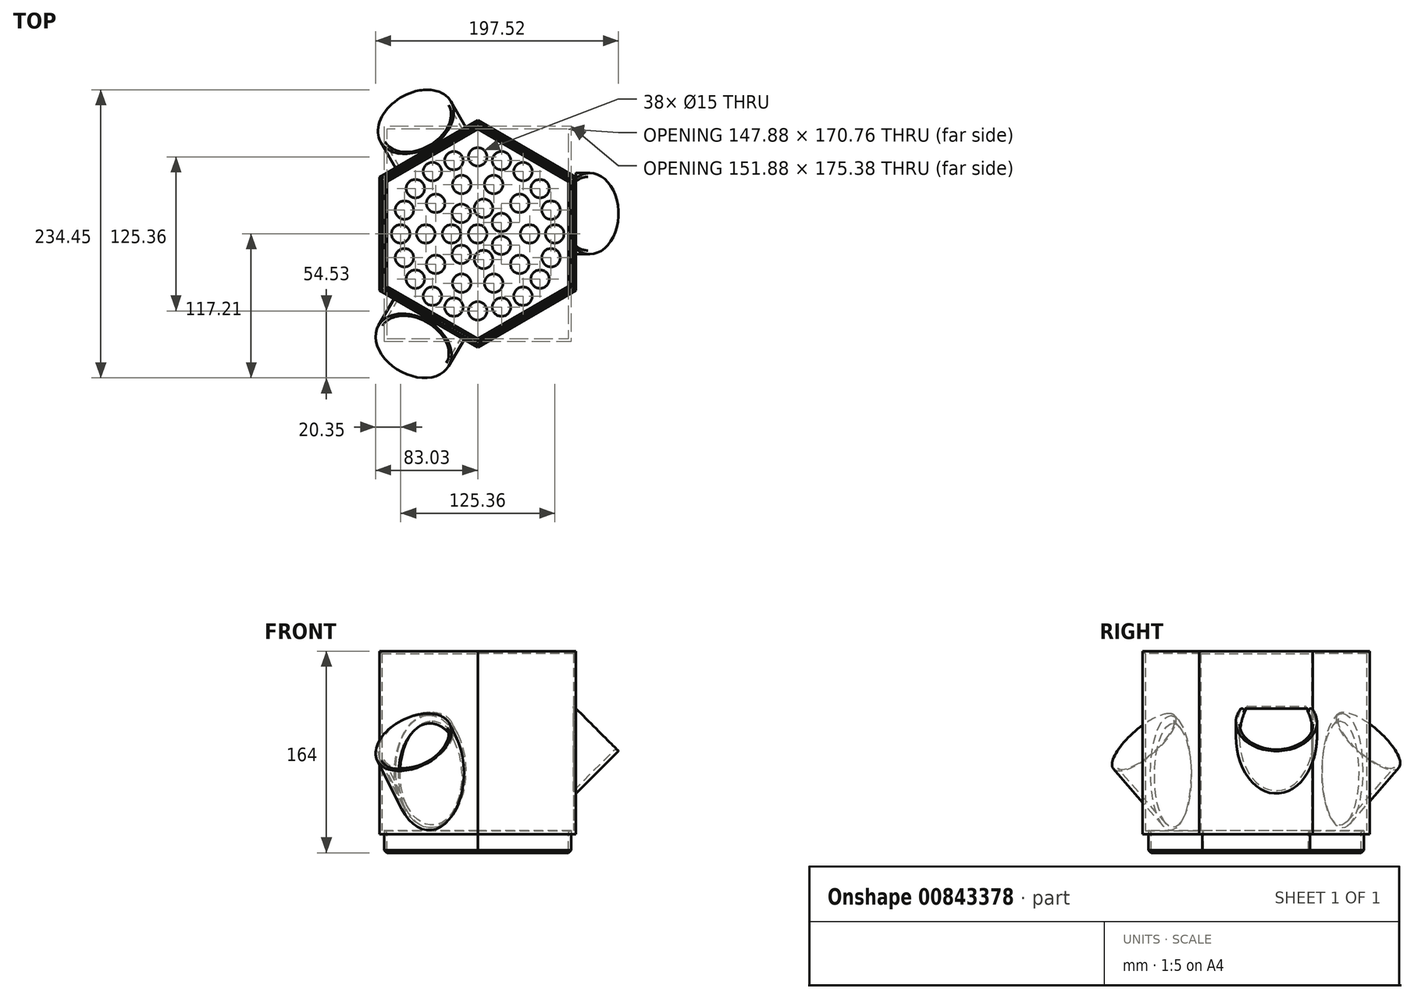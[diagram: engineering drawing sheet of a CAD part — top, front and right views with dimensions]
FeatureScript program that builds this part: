
annotation { "Feature Type Name" : "Feature", "Feature Type Description" : "" }
export const myFeature = defineFeature(function(context is Context, id is Id, definition is map)
    precondition{}
    {
        {
            var Q0;
            Q0=qCreatedBy(makeId("Top.planeOp"),FACE);
            var sketch = newSketch(context, id + "F0", { "sketchPlane" : qUnion([Q0])});
            skCircle(sketch, "E0.cCircle", {"center": v(0, 0) * mm, "radius": 77.94 * mm, "construction": true});
            skLineSegment(sketch, "E0.0", {"start": v(-77.94, -45) * mm, "end": v(-77.94, 45) * mm});
            skLineSegment(sketch, "E0.1", {"start": v(-77.94, 45) * mm, "end": v(0, 90) * mm});
            skLineSegment(sketch, "E0.2", {"start": v(0, 90) * mm, "end": v(77.94, 45) * mm});
            skLineSegment(sketch, "E0.3", {"start": v(77.94, 45) * mm, "end": v(77.94, -45) * mm});
            skLineSegment(sketch, "E0.4", {"start": v(77.94, -45) * mm, "end": v(0, -90) * mm});
            skLineSegment(sketch, "E0.5", {"start": v(0, -90) * mm, "end": v(-77.94, -45) * mm});
            skPoint(sketch, "E0.0.midPoint", {"position": v(-77.94, 0) * mm});
            skLineSegment(sketch, "E1.0", {"start": v(-79.94, -46.15) * mm, "end": v(-79.94, 46.15) * mm});
            skLineSegment(sketch, "E1.1", {"start": v(0, 92.3) * mm, "end": v(79.94, 46.15) * mm});
            skLineSegment(sketch, "E1.2", {"start": v(79.94, 46.15) * mm, "end": v(79.94, -46.15) * mm});
            skLineSegment(sketch, "E1.3", {"start": v(-79.94, 46.15) * mm, "end": v(0, 92.3) * mm});
            skLineSegment(sketch, "E1.4", {"start": v(79.94, -46.15) * mm, "end": v(0, -92.3) * mm});
            skLineSegment(sketch, "E1.5", {"start": v(0, -92.3) * mm, "end": v(-79.94, -46.15) * mm});
            skLineSegment(sketch, "E2.0", {"start": v(73.94, -42.7) * mm, "end": v(0, -85.38) * mm});
            skLineSegment(sketch, "E2.1", {"start": v(-73.94, -42.7) * mm, "end": v(-73.94, 42.7) * mm});
            skLineSegment(sketch, "E2.2", {"start": v(-73.94, 42.7) * mm, "end": v(0, 85.38) * mm});
            skLineSegment(sketch, "E2.3", {"start": v(0, -85.38) * mm, "end": v(-73.94, -42.7) * mm});
            skLineSegment(sketch, "E2.4", {"start": v(0, 85.38) * mm, "end": v(73.94, 42.7) * mm});
            skLineSegment(sketch, "E2.5", {"start": v(73.94, 42.7) * mm, "end": v(73.94, -42.7) * mm});
            skLineSegment(sketch, "E3.0", {"start": v(75.94, 43.85) * mm, "end": v(75.94, -43.85) * mm});
            skLineSegment(sketch, "E3.1", {"start": v(0, -87.7) * mm, "end": v(-75.94, -43.85) * mm});
            skLineSegment(sketch, "E3.2", {"start": v(-75.94, -43.85) * mm, "end": v(-75.94, 43.85) * mm});
            skLineSegment(sketch, "E3.3", {"start": v(75.94, -43.85) * mm, "end": v(0, -87.7) * mm});
            skLineSegment(sketch, "E3.4", {"start": v(-75.94, 43.85) * mm, "end": v(0, 87.7) * mm});
            skLineSegment(sketch, "E3.5", {"start": v(0, 87.7) * mm, "end": v(75.94, 43.85) * mm});
            skCircle(sketch, "E4", {"center": v(0, 0) * mm, "radius": 7.5 * mm});
            skLineSegment(sketch, "E5", {"start": v(0, 0) * mm, "end": v(-77.94, 0) * mm, "construction": true});
            skCircle(sketch, "E6", {"center": v(-21.35, 0) * mm, "radius": 7.5 * mm});
            skCircle(sketch, "E7", {"center": v(-62.68, 0) * mm, "radius": 7.5 * mm});
            skCircle(sketch, "E8", {"center": v(-42.22, 0) * mm, "radius": 7.5 * mm});
            skCircle(sketch, "E9.1.0", {"center": v(-13.31, -16.7) * mm, "radius": 7.5 * mm});
            skCircle(sketch, "E9.2.0", {"center": v(4.75, -20.82) * mm, "radius": 7.5 * mm});
            skCircle(sketch, "E9.3.0", {"center": v(19.24, -9.27) * mm, "radius": 7.5 * mm});
            skCircle(sketch, "E9.4.0", {"center": v(19.24, 9.27) * mm, "radius": 7.5 * mm});
            skCircle(sketch, "E9.5.0", {"center": v(4.75, 20.82) * mm, "radius": 7.5 * mm});
            skCircle(sketch, "E9.6.0", {"center": v(-13.31, 16.7) * mm, "radius": 7.5 * mm});
            skCircle(sketch, "E10.1.0", {"center": v(-34.16, -24.82) * mm, "radius": 7.5 * mm});
            skCircle(sketch, "E10.2.0", {"center": v(-13.05, -40.15) * mm, "radius": 7.5 * mm});
            skCircle(sketch, "E10.3.0", {"center": v(13.05, -40.15) * mm, "radius": 7.5 * mm});
            skCircle(sketch, "E10.4.0", {"center": v(34.16, -24.82) * mm, "radius": 7.5 * mm});
            skCircle(sketch, "E10.5.0", {"center": v(42.22, 0) * mm, "radius": 7.5 * mm});
            skCircle(sketch, "E10.6.0", {"center": v(34.16, 24.82) * mm, "radius": 7.5 * mm});
            skCircle(sketch, "E10.7.0", {"center": v(13.05, 40.15) * mm, "radius": 7.5 * mm});
            skCircle(sketch, "E10.8.0", {"center": v(-13.05, 40.15) * mm, "radius": 7.5 * mm});
            skCircle(sketch, "E10.9.0", {"center": v(-34.16, 24.82) * mm, "radius": 7.5 * mm});
            skCircle(sketch, "E11.1.0", {"center": v(-59.61, -19.37) * mm, "radius": 7.5 * mm});
            skCircle(sketch, "E11.2.0", {"center": v(-50.7, -36.84) * mm, "radius": 7.5 * mm});
            skCircle(sketch, "E11.3.0", {"center": v(-36.84, -50.7) * mm, "radius": 7.5 * mm});
            skCircle(sketch, "E11.4.0", {"center": v(-19.37, -59.61) * mm, "radius": 7.5 * mm});
            skCircle(sketch, "E11.5.0", {"center": v(0, -62.68) * mm, "radius": 7.5 * mm});
            skCircle(sketch, "E11.6.0", {"center": v(19.37, -59.61) * mm, "radius": 7.5 * mm});
            skCircle(sketch, "E11.7.0", {"center": v(36.84, -50.7) * mm, "radius": 7.5 * mm});
            skCircle(sketch, "E11.8.0", {"center": v(50.7, -36.84) * mm, "radius": 7.5 * mm});
            skCircle(sketch, "E11.9.0", {"center": v(59.61, -19.37) * mm, "radius": 7.5 * mm});
            skCircle(sketch, "E12.1.10.0", {"center": v(62.68, 0) * mm, "radius": 7.5 * mm});
            skCircle(sketch, "E12.1.11.0", {"center": v(59.61, 19.37) * mm, "radius": 7.5 * mm});
            skCircle(sketch, "E12.1.12.0", {"center": v(50.7, 36.84) * mm, "radius": 7.5 * mm});
            skCircle(sketch, "E12.1.13.0", {"center": v(36.84, 50.7) * mm, "radius": 7.5 * mm});
            skCircle(sketch, "E12.1.14.0", {"center": v(19.37, 59.61) * mm, "radius": 7.5 * mm});
            skCircle(sketch, "E12.1.15.0", {"center": v(0, 62.68) * mm, "radius": 7.5 * mm});
            skCircle(sketch, "E12.1.16.0", {"center": v(-19.37, 59.61) * mm, "radius": 7.5 * mm});
            skCircle(sketch, "E12.1.17.0", {"center": v(-36.84, 50.7) * mm, "radius": 7.5 * mm});
            skCircle(sketch, "E12.1.18.0", {"center": v(-50.7, 36.84) * mm, "radius": 7.5 * mm});
            skCircle(sketch, "E12.1.19.0", {"center": v(-59.61, 19.37) * mm, "radius": 7.5 * mm});
            skSolve(sketch);
        }
        {
            var Q0;
            Q0 = qSketchRegion(id + "F0", true);
            extrude(context, id + "F1", {"entities" : qUnion([Q0]), "depth" : 150 * mm, "offsetDistance" : 25 * mm});
        }
        {
            var Q0;
            Q0=makeQuery(id+"F1.opExtrude","SWEPT_FACE",FACE,{"disambiguationData":[OSD([sQuery(id+"F0.wireOp",EDGE,"E1.2")])]});
            cPlane(context, id + "F2", {"entities" : qUnion([Q0]), "cplaneType" : CPlaneType.OFFSET, "offset" : 25 * mm, "width" : 150 * mm, "height" : 150 * mm});
        }
        {
            var Q0;
            Q0=qCreatedBy(id+"F2.planeOp",FACE);
            var sketch = newSketch(context, id + "F3", { "sketchPlane" : qUnion([Q0])});
            skLineSegment(sketch, "E13", {"start": v(-46.09, 77.36) * mm, "end": v(45.67, 77.36) * mm, "construction": true});
            skSolve(sketch);
        }
        {
            var Q0;
            Q0=sQuery(id+"F3.wireOp",EDGE,"E13");
            cPlane(context, id + "F4", {"entities" : qUnion([Q0]), "cplaneType" : CPlaneType.LINE_ANGLE, "offset" : 25 * mm, "angle" : 45 * degree, "width" : 150 * mm, "height" : 150 * mm});
        }
        {
            var Q0;
            Q0=qCreatedBy(id+"F4.planeOp",FACE);
            var sketch = newSketch(context, id + "F5", { "sketchPlane" : qUnion([Q0])});
            skCircle(sketch, "E14", {"center": v(16.48, 0) * mm, "radius": 30 * mm});
            skCircle(sketch, "E15.0", {"center": v(16.48, 0) * mm, "radius": 33 * mm});
            skSolve(sketch);
        }
        {
            var Q0;
            Q0=makeQuery(id+"F5.imprint","IMPRINT",FACE,{"disambiguationData":[TD([[makeQuery(id+"F5.imprint","IMPRINT",EDGE,{"derivedFrom":sQuery(id+"F5.wireOp",EDGE,"E14")}),-1.0]])]});
            var Q1;
            Q1=makeQuery(id+"F1.opExtrude","SWEPT_FACE",FACE,{"disambiguationData":[OSD([sQuery(id+"F0.wireOp",EDGE,"E1.2")])]});
            extrude(context, id + "F6", {"entities" : qUnion([Q0]), "operationType" : NewBodyOperationType.ADD, "endBound" : BoundingType.UP_TO_SURFACE, "oppositeDirection" : true, "depth" : 25 * mm, "endBoundEntityFace" : qUnion([Q1]), "offsetDistance" : 25 * mm});
        }
        {
            var Q0;
            Q0=makeQuery(id+"F5.imprint","IMPRINT",FACE,{"disambiguationData":[TD([[makeQuery(id+"F5.imprint","IMPRINT",EDGE,{"derivedFrom":sQuery(id+"F5.wireOp",EDGE,"E14")}),1.0]])]});
            var Q1;
            Q1=makeQuery(id+"F1.opExtrude","SWEPT_FACE",FACE,{"disambiguationData":[OSD([sQuery(id+"F0.wireOp",EDGE,"E0.3")])]});
            extrude(context, id + "F7", {"entities" : qUnion([Q0]), "operationType" : NewBodyOperationType.REMOVE, "endBound" : BoundingType.UP_TO_SURFACE, "oppositeDirection" : true, "depth" : 25 * mm, "endBoundEntityFace" : qUnion([Q1]), "offsetDistance" : 25 * mm});
        }
        {
            var Q0;
            Q0=makeQuery(id+"F1.opExtrude","SWEPT_FACE",FACE,{"disambiguationData":[OSD([sQuery(id+"F0.wireOp",EDGE,"E1.3")])]});
            cPlane(context, id + "F8", {"entities" : qUnion([Q0]), "cplaneType" : CPlaneType.OFFSET, "offset" : 25 * mm, "width" : 150 * mm, "height" : 150 * mm});
        }
        {
            var Q0;
            Q0=qCreatedBy(id+"F8.planeOp",FACE);
            var sketch = newSketch(context, id + "F9", { "sketchPlane" : qUnion([Q0])});
            skLineSegment(sketch, "E16", {"start": v(-47.86, 75) * mm, "end": v(44.27, 75) * mm, "construction": true});
            skSolve(sketch);
        }
        {
            var Q0;
            Q0=sQuery(id+"F9.wireOp",EDGE,"E16");
            cPlane(context, id + "F10", {"entities" : qUnion([Q0]), "cplaneType" : CPlaneType.LINE_ANGLE, "offset" : 25 * mm, "angle" : 45 * degree, "oppositeDirection" : true, "width" : 150 * mm, "height" : 150 * mm});
        }
        {
            var Q0;
            Q0=qCreatedBy(id+"F10.planeOp",FACE);
            var sketch = newSketch(context, id + "F11", { "sketchPlane" : qUnion([Q0])});
            skCircle(sketch, "E17", {"center": v(-5.63, -19.23) * mm, "radius": 30 * mm});
            skCircle(sketch, "E18.0", {"center": v(-5.63, -19.23) * mm, "radius": 33 * mm});
            skSolve(sketch);
        }
        {
            var Q0;
            Q0 = qSketchRegion(id + "F11", true);
            var Q1;
            Q1=makeQuery(id+"F1.opExtrude","SWEPT_FACE",FACE,{"disambiguationData":[OSD([sQuery(id+"F0.wireOp",EDGE,"E1.3")])]});
            extrude(context, id + "F12", {"entities" : qUnion([Q0]), "operationType" : NewBodyOperationType.ADD, "endBound" : BoundingType.UP_TO_SURFACE, "depth" : 25 * mm, "endBoundEntityFace" : qUnion([Q1]), "offsetDistance" : 25 * mm});
        }
        {
            var Q0;
            Q0=makeQuery(id+"F11.imprint","IMPRINT",FACE,{"disambiguationData":[TD([[makeQuery(id+"F11.imprint","IMPRINT",EDGE,{"derivedFrom":sQuery(id+"F11.wireOp",EDGE,"E17")}),1.0]])]});
            var Q1;
            Q1=makeQuery(id+"F1.opExtrude","SWEPT_FACE",FACE,{"disambiguationData":[OSD([sQuery(id+"F0.wireOp",EDGE,"E0.1")])]});
            extrude(context, id + "F13", {"entities" : qUnion([Q0]), "operationType" : NewBodyOperationType.REMOVE, "endBound" : BoundingType.UP_TO_SURFACE, "depth" : 25 * mm, "endBoundEntityFace" : qUnion([Q1]), "offsetDistance" : 25 * mm});
        }
        {
            var Q0;
            Q0=makeQuery(id+"F1.opExtrude","SWEPT_FACE",FACE,{"disambiguationData":[OSD([sQuery(id+"F0.wireOp",EDGE,"E1.5")])]});
            cPlane(context, id + "F14", {"entities" : qUnion([Q0]), "cplaneType" : CPlaneType.OFFSET, "offset" : 25 * mm, "width" : 150 * mm, "height" : 150 * mm});
        }
        {
            var Q0;
            Q0=qCreatedBy(id+"F14.planeOp",FACE);
            var sketch = newSketch(context, id + "F15", { "sketchPlane" : qUnion([Q0])});
            skLineSegment(sketch, "E19", {"start": v(-42.7, 75) * mm, "end": v(45.48, 75) * mm, "construction": true});
            skSolve(sketch);
        }
        {
            var Q0;
            Q0=sQuery(id+"F15.wireOp",EDGE,"E19");
            cPlane(context, id + "F16", {"entities" : qUnion([Q0]), "cplaneType" : CPlaneType.LINE_ANGLE, "offset" : 25 * mm, "angle" : 315 * degree, "width" : 150 * mm, "height" : 150 * mm});
        }
        {
            var Q0;
            Q0=qCreatedBy(id+"F16.planeOp",FACE);
            var sketch = newSketch(context, id + "F17", { "sketchPlane" : qUnion([Q0])});
            skCircle(sketch, "E20", {"center": v(-7.67, 19.81) * mm, "radius": 30 * mm});
            skCircle(sketch, "E21.0", {"center": v(-7.67, 19.81) * mm, "radius": 33 * mm});
            skSolve(sketch);
        }
        {
            var Q0;
            Q0 = qSketchRegion(id + "F17", true);
            var Q1;
            Q1=makeQuery(id+"F1.opExtrude","SWEPT_FACE",FACE,{"disambiguationData":[OSD([sQuery(id+"F0.wireOp",EDGE,"E1.5")])]});
            extrude(context, id + "F18", {"entities" : qUnion([Q0]), "operationType" : NewBodyOperationType.ADD, "endBound" : BoundingType.UP_TO_SURFACE, "depth" : 25 * mm, "endBoundEntityFace" : qUnion([Q1]), "offsetDistance" : 25 * mm});
        }
        {
            var Q0;
            Q0=makeQuery(id+"F17.imprint","IMPRINT",FACE,{"disambiguationData":[TD([[makeQuery(id+"F17.imprint","IMPRINT",EDGE,{"derivedFrom":sQuery(id+"F17.wireOp",EDGE,"E20")}),1.0]])]});
            var Q1;
            Q1=makeQuery(id+"F1.opExtrude","SWEPT_FACE",FACE,{"disambiguationData":[OSD([sQuery(id+"F0.wireOp",EDGE,"E0.5")])]});
            extrude(context, id + "F19", {"entities" : qUnion([Q0]), "operationType" : NewBodyOperationType.REMOVE, "endBound" : BoundingType.UP_TO_SURFACE, "depth" : 25 * mm, "endBoundEntityFace" : qUnion([Q1]), "offsetDistance" : 25 * mm});
        }
        {
            var Q0;
            Q0=makeQuery(id+"F0.imprint","IMPRINT",FACE,{"disambiguationData":[TD([[makeQuery(id+"F0.imprint","IMPRINT",EDGE,{"derivedFrom":sQuery(id+"F0.wireOp",EDGE,"E0.0")}),-1.0]])]});
            extrude(context, id + "F20", {"entities" : qUnion([Q0]), "operationType" : NewBodyOperationType.ADD, "depth" : 3 * mm, "offsetDistance" : 25 * mm});
        }
        {
            var Q0;
            Q0=makeQuery(id+"F0.imprint","IMPRINT",FACE,{"disambiguationData":[TD([[makeQuery(id+"F0.imprint","IMPRINT",EDGE,{"derivedFrom":sQuery(id+"F0.wireOp",EDGE,"E2.0")}),1.0]])]});
            extrude(context, id + "F21", {"entities" : qUnion([Q0]), "oppositeDirection" : true, "depth" : 15 * mm, "offsetDistance" : 25 * mm});
        }
        {
            var Q0;
            Q0=makeQuery(id+"F0.imprint","IMPRINT",FACE,{"disambiguationData":[TD([[makeQuery(id+"F0.imprint","IMPRINT",EDGE,{"derivedFrom":sQuery(id+"F0.wireOp",EDGE,"E2.0")}),-1.0]])]});
            extrude(context, id + "F22", {"entities" : qUnion([Q0]), "operationType" : NewBodyOperationType.ADD, "oppositeDirection" : true, "depth" : 15 * mm, "offsetDistance" : 25 * mm});
        }
        {
            var Q0;
            Q0=makeQuery(id+"F0.imprint","IMPRINT",FACE,{"disambiguationData":[TD([[makeQuery(id+"F0.imprint","IMPRINT",EDGE,{"derivedFrom":sQuery(id+"F0.wireOp",EDGE,"E2.0")}),-1.0]])]});
            extrude(context, id + "F23", {"entities" : qUnion([Q0]), "operationType" : NewBodyOperationType.REMOVE, "oppositeDirection" : true, "depth" : 13 * mm, "offsetDistance" : 25 * mm});
        }
        {
            var Q0;
            Q0=makeQuery(id+"F0.imprint","IMPRINT",FACE,{"disambiguationData":[TD([[makeQuery(id+"F0.imprint","IMPRINT",EDGE,{"derivedFrom":sQuery(id+"F0.wireOp",EDGE,"E2.0")}),1.0]])]});
            extrude(context, id + "F24", {"entities" : qUnion([Q0]), "depth" : 3 * mm, "offsetDistance" : 25 * mm});
        }
        {
            var Q0;
            Q0=makeQuery(id+"F1.opExtrude","CAP_EDGE",EDGE,{"disambiguationData":[OSD([sQuery(id+"F0.wireOp",EDGE,"E0.3")])],"isStart":false});
            var Q1;
            Q1=makeQuery(id+"F1.opExtrude","CAP_EDGE",EDGE,{"disambiguationData":[OSD([sQuery(id+"F0.wireOp",EDGE,"E0.4")])],"isStart":false});
            var Q2;
            Q2=makeQuery(id+"F1.opExtrude","CAP_EDGE",EDGE,{"disambiguationData":[OSD([sQuery(id+"F0.wireOp",EDGE,"E0.5")])],"isStart":false});
            var Q3;
            Q3=makeQuery(id+"F1.opExtrude","CAP_EDGE",EDGE,{"disambiguationData":[OSD([sQuery(id+"F0.wireOp",EDGE,"E0.0")])],"isStart":false});
            var Q4;
            Q4=makeQuery(id+"F1.opExtrude","CAP_EDGE",EDGE,{"disambiguationData":[OSD([sQuery(id+"F0.wireOp",EDGE,"E0.1")])],"isStart":false});
            var Q5;
            Q5=makeQuery(id+"F1.opExtrude","CAP_EDGE",EDGE,{"disambiguationData":[OSD([sQuery(id+"F0.wireOp",EDGE,"E0.2")])],"isStart":false});
            chamfer(context, id + "F25", {"entities" : qUnion([Q0, Q1, Q2, Q3, Q4, Q5]), "width" : 3 * mm, "tangentPropagation" : true});
        }
        {
            var Q0;
            Q0=makeQuery(id+"F12.opExtrude","CAP_EDGE",EDGE,{"disambiguationData":[OSD([sQuery(id+"F11.wireOp",EDGE,"E17")])],"isStart":true});
            var Q1;
            Q1=makeQuery(id+"F18.opExtrude","CAP_EDGE",EDGE,{"disambiguationData":[OSD([sQuery(id+"F17.wireOp",EDGE,"E20")])],"isStart":true});
            var Q2;
            Q2=makeQuery(id+"F6.opExtrude","CAP_EDGE",EDGE,{"disambiguationData":[OSD([sQuery(id+"F5.wireOp",EDGE,"E14")])],"isStart":true});
            var Q3;
            Q3=makeQuery(id+"F24.opExtrude","CAP_EDGE",EDGE,{"disambiguationData":[OSD([sQuery(id+"F0.wireOp",EDGE,"E2.5")])],"isStart":false});
            var Q4;
            Q4=makeQuery(id+"F24.opExtrude","CAP_EDGE",EDGE,{"disambiguationData":[OSD([sQuery(id+"F0.wireOp",EDGE,"E2.0")])],"isStart":false});
            var Q5;
            Q5=makeQuery(id+"F24.opExtrude","CAP_EDGE",EDGE,{"disambiguationData":[OSD([sQuery(id+"F0.wireOp",EDGE,"E2.4")])],"isStart":false});
            var Q6;
            Q6=makeQuery(id+"F24.opExtrude","CAP_EDGE",EDGE,{"disambiguationData":[OSD([sQuery(id+"F0.wireOp",EDGE,"E2.1")])],"isStart":false});
            var Q7;
            Q7=makeQuery(id+"F24.opExtrude","CAP_EDGE",EDGE,{"disambiguationData":[OSD([sQuery(id+"F0.wireOp",EDGE,"E2.2")])],"isStart":false});
            var Q8;
            Q8=makeQuery(id+"F24.opExtrude","CAP_EDGE",EDGE,{"disambiguationData":[OSD([sQuery(id+"F0.wireOp",EDGE,"E2.3")])],"isStart":false});
            fillet(context, id + "F26", {"entities" : qUnion([Q0, Q1, Q2, Q3, Q4, Q5, Q6, Q7, Q8]), "radius" : 2 * mm, "tangentPropagation" : true, "allowEdgeOverflow" : false});
        }
        {
            var Q0;
            Q0=makeQuery(id+"F21.opExtrude","CAP_EDGE",EDGE,{"disambiguationData":[OSD([sQuery(id+"F0.wireOp",EDGE,"E3.0")])],"isStart":false});
            var Q1;
            Q1=makeQuery(id+"F21.opExtrude","CAP_EDGE",EDGE,{"disambiguationData":[OSD([sQuery(id+"F0.wireOp",EDGE,"E3.5")])],"isStart":false});
            var Q2;
            Q2=makeQuery(id+"F21.opExtrude","CAP_EDGE",EDGE,{"disambiguationData":[OSD([sQuery(id+"F0.wireOp",EDGE,"E3.4")])],"isStart":false});
            var Q3;
            Q3=makeQuery(id+"F21.opExtrude","CAP_EDGE",EDGE,{"disambiguationData":[OSD([sQuery(id+"F0.wireOp",EDGE,"E3.2")])],"isStart":false});
            var Q4;
            Q4=makeQuery(id+"F21.opExtrude","CAP_EDGE",EDGE,{"disambiguationData":[OSD([sQuery(id+"F0.wireOp",EDGE,"E3.1")])],"isStart":false});
            var Q5;
            Q5=makeQuery(id+"F21.opExtrude","CAP_EDGE",EDGE,{"disambiguationData":[OSD([sQuery(id+"F0.wireOp",EDGE,"E3.3")])],"isStart":false});
            chamfer(context, id + "F27", {"entities" : qUnion([Q0, Q1, Q2, Q3, Q4, Q5]), "width" : 2 * mm, "tangentPropagation" : true});
        }
    });
